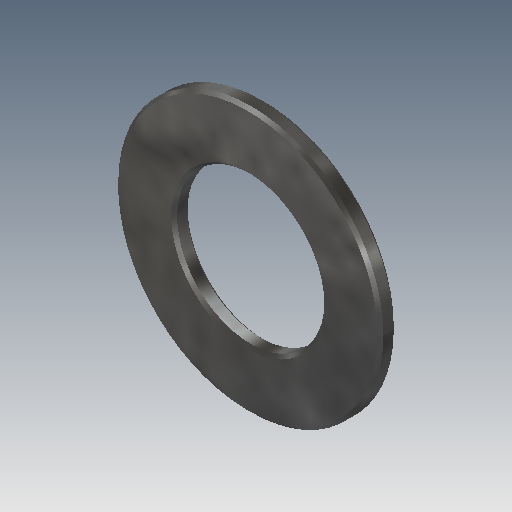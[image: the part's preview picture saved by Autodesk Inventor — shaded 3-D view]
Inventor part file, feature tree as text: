
AUTODESK INVENTOR PART (.ipt)
format: ipt  version: 2018 (Build 220112000, 112)  size: 138,240 bytes
history: native  units: mm
features: extrude x1, chamfer x1, sketch x1
ambient origin geometry x8: Origin, YZ Plane, XZ Plane, XY Plane, X Axis, Y Axis, Z Axis, Center Point
bodies: Solid1 (feature_tree)
feature tree (3):
  extrude  "Extrusion1"  Depth=1.1mm
  chamfer  "Chamfer1"  Distance=1.1mm
  sketch  "Sketch1"  dims[d0=10.0mm d1=18.0mm d2=1.1mm d3=0.0mm d4=0.2mm d5=2.0mm d6=45.0deg]
